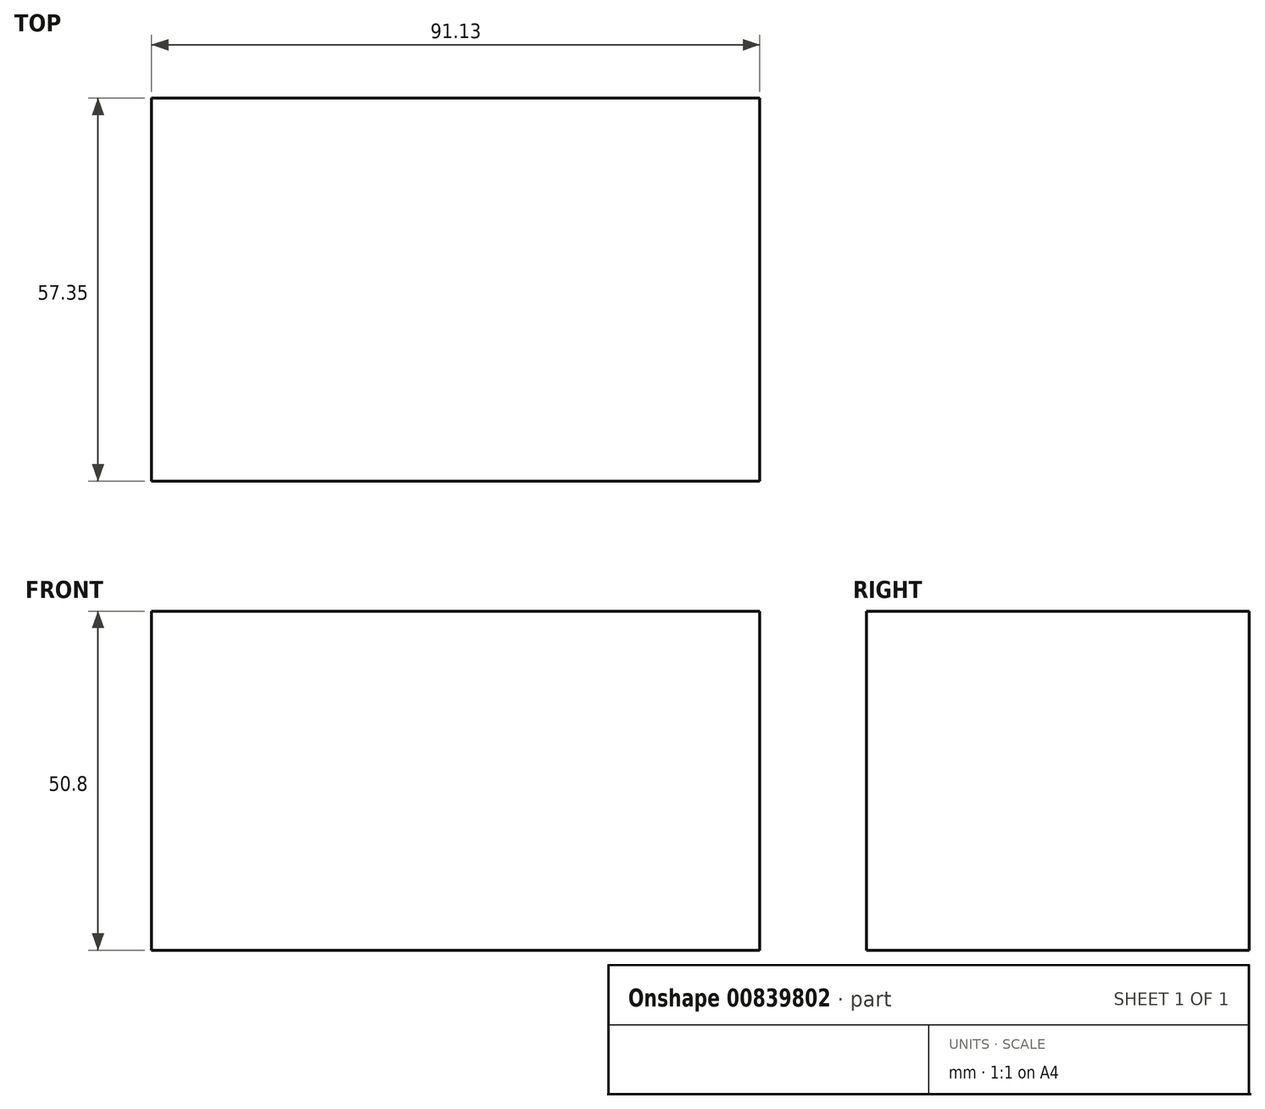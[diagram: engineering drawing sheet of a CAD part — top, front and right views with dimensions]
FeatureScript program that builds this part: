
annotation { "Feature Type Name" : "Feature", "Feature Type Description" : "" }
export const myFeature = defineFeature(function(context is Context, id is Id, definition is map)
    precondition{}
    {
        {
            var Q0;
            Q0=qCreatedBy(makeId("Top.planeOp"),FACE);
            var sketch = newSketch(context, id + "F0", { "sketchPlane" : qUnion([Q0])});
            skLineSegment(sketch, "E0.bottom", {"start": v(-49.8, 32.13) * mm, "end": v(41.34, 32.13) * mm});
            skLineSegment(sketch, "E0.top", {"start": v(-49.8, -25.22) * mm, "end": v(41.34, -25.22) * mm});
            skLineSegment(sketch, "E0.left", {"start": v(-49.8, 32.13) * mm, "end": v(-49.8, -25.22) * mm});
            skLineSegment(sketch, "E0.right", {"start": v(41.34, 32.13) * mm, "end": v(41.34, -25.22) * mm});
            skLineSegment(sketch, "E1.0", {"start": v(-62.5, 44.83) * mm, "end": v(54.04, 44.83) * mm, "construction": true});
            skLineSegment(sketch, "E1.1", {"start": v(-62.5, 44.83) * mm, "end": v(-62.5, -37.92) * mm, "construction": true});
            skLineSegment(sketch, "E1.2", {"start": v(-62.5, -37.92) * mm, "end": v(54.04, -37.92) * mm, "construction": true});
            skLineSegment(sketch, "E1.3", {"start": v(54.04, 44.83) * mm, "end": v(54.04, -37.92) * mm, "construction": true});
            skLineSegment(sketch, "E2.0", {"start": v(-49.8, 25.78) * mm, "end": v(41.34, 25.78) * mm, "construction": true});
            skSolve(sketch);
        }
        {
            var Q0;
            Q0 = qSketchRegion(id + "F0", true);
            extrude(context, id + "F1", {"entities" : qUnion([Q0]), "depth" : 50.8 * mm, "offsetDistance" : 25.4 * mm});
        }
    });
